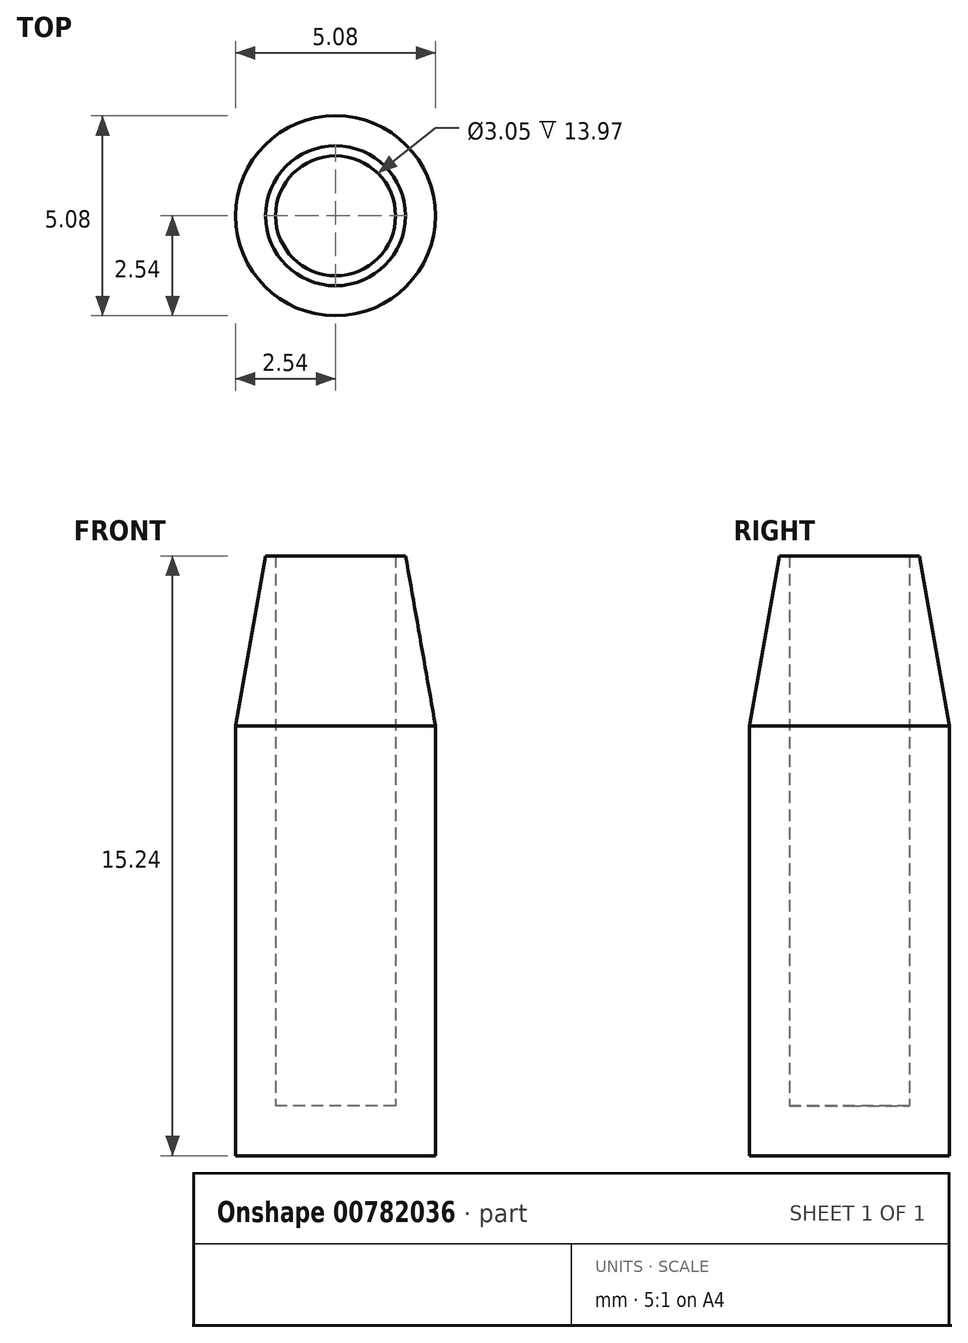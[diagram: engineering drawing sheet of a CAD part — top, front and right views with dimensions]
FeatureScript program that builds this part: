
annotation { "Feature Type Name" : "Feature", "Feature Type Description" : "" }
export const myFeature = defineFeature(function(context is Context, id is Id, definition is map)
    precondition{}
    {
        {
            var Q0;
            Q0=qCreatedBy(makeId("Top.planeOp"),FACE);
            var sketch = newSketch(context, id + "F0", { "sketchPlane" : qUnion([Q0])});
            skCircle(sketch, "E0", {"center": v(0, 0) * mm, "radius": 2.54 * mm});
            skSolve(sketch);
        }
        {
            var Q0;
            Q0=makeQuery(id+"F0.imprint","IMPRINT",FACE,{"disambiguationData":[TD([[makeQuery(id+"F0.imprint","IMPRINT",EDGE,{"derivedFrom":sQuery(id+"F0.wireOp",EDGE,"E0")}),1.0]])]});
            extrude(context, id + "F1", {"entities" : qUnion([Q0]), "depth" : 1.27 * mm, "offsetDistance" : 25.4 * mm});
        }
        {
            var Q0;
            Q0=makeQuery(id+"F1.opExtrude","CAP_FACE",FACE,{"disambiguationData":[OSD([sQuery(id+"F0.wireOp",EDGE,"E0")])],"isStart":false});
            var sketch = newSketch(context, id + "F2", { "sketchPlane" : qUnion([Q0])});
            skCircle(sketch, "E1", {"center": v(0, 0) * mm, "radius": 1.52 * mm});
            skSolve(sketch);
        }
        {
            var Q0;
            Q0=makeQuery(id+"F2.imprint","IMPRINT",FACE,{"disambiguationData":[TD([[makeQuery(id+"F2.imprint","IMPRINT",EDGE,{"derivedFrom":sQuery(id+"F2.wireOp",EDGE,"E1")}),-1.0]])]});
            extrude(context, id + "F3", {"entities" : qUnion([Q0]), "operationType" : NewBodyOperationType.ADD, "depth" : 13.97 * mm, "offsetDistance" : 25.4 * mm});
        }
        {
            var Q0;
            Q0=makeQuery(id+"F3.opExtrude","CAP_EDGE",EDGE,{"disambiguationData":[OSD([sQuery(id+"F0.wireOp",EDGE,"E0")])],"isStart":false});
            chamfer(context, id + "F4", {"entities" : qUnion([Q0]), "chamferType" : ChamferType.OFFSET_ANGLE, "width" : 0.76 * mm, "oppositeDirection" : false, "angle" : 80 * degree, "tangentPropagation" : true});
        }
    });
